# Revit family: Essentials Cupoard
name_source: partatom
category: Furniture
revit_build: Autodesk Revit 2018 (Build: 20190510_1515(x64)
units: mm (PartAtom-declared; Revit-internal decimal feet)

## family parameters
Always vertical = Yes
Cut with Voids When Loaded = No
OmniClass Number = 23.40.20.00
OmniClass Title = General Furniture and Specialties
Room Calculation Point = No
Shared = No
Work Plane-Based = No

## types (19) — shared parameters
Colour = Classic
Compliance Standards Certification = BS EN 14073-2:2004 Parts 2 and 3 and BS EN 14074:2004
Depth = 470 mm  [stored 1.54199 ft]
Expected Life = >5 years
Finish = Powder coated Steel
Manufacturer = Bisley
Range = Essentals
Revision = V1
Routine Maintenance = We recommend you clean your unit with warm water and a mild detergent solution. A damp cloth can be used to remove dust particles.
Uniclass 2015 Code = PR_40_30_78_57
Uniclass2015Title = Shelves and Storage Units
Uniclass2015Version = V1.13
Warranty = 5 Years

## per-type parameters (varying)
| type | Carcass Size | Carcass_Material | Door size | Door_Material | Height | Model | Model Reference | URL | Width |
| YECB0807 | Carcass : YECB0807 | Steel, Mild | Doors : YECB0807 | Steel, Mild | 693 mm  [stored 2.27362 ft] | YECB0907 | YECB0907 | www.bisley.com | 800 mm  [stored 2.62467 ft] |
| YECBDH0807 | Carcass : YECBDH0807 | Steel, Mild | Doors : YECBDH0807 | Steel, Mild | 718 mm  [stored 2.35564 ft] | YECB0807 | YECB0807 | www.bisley.com | 800 mm  [stored 2.62467 ft] |
| YECB0810 | Carcass : YECB0810 | Steel, Mild | Doors : YECB0810 | Steel, Mild | 1000 mm  [stored 3.28084 ft] | YECB0810 | YECB0810 | WWW.BISLEY.COM | 800 mm  [stored 2.62467 ft] |
| YECB0811 | Carcass : YECB0811 | Steel, Mild | Doors : YECB0811 | Steel, Mild | 1070 mm  [stored 3.5105 ft] | YECB0811 | YECB0811 | www.bisley.com | 800 mm  [stored 2.62467 ft] |
| YECB0812 | Carcass : YECB0812 | Steel, Mild | Doors : YECB0812 | Steel, Mild | 1270 mm | YECB0812 | YECB0812 | www.bisley.com | 800 mm  [stored 2.62467 ft] |
| YECB0815 | Carcass : YECB0815 | Steel, Mild | Doors : YECB0815 | Steel, Mild | 1570 mm | YECB0815 | YECB0815 | www.bisley.com | 800 mm  [stored 2.62467 ft] |
| YECB0819 | Carcass : YECB0819 | Steel, Mild | Doors : YECB0819 | Steel, Mild | 1970 mm  [stored 6.46325 ft] | YECB0919 | YECB0919 | www.bisley.com | 800 mm  [stored 2.62467 ft] |
| YECB0910 | Carcass : YECB0910 | <By Category> | Doors : YECB0910 | <By Category> | 1000 mm  [stored 3.28084 ft] | YECB0910 | YECB0910 | www.bisley.com | 900 mm  [stored 2.95276 ft] |
| YECB0911 | Carcass : YECB0911 | Steel, Mild | Doors : YECB0911 | Steel, Mild | 1070 mm  [stored 3.5105 ft] | YECB0911 | YECB0911 | www.bisley.com | 900 mm  [stored 2.95276 ft] |
| YECB0912 | Carcass : YECB0912 | Steel, Mild | Doors : YECB0912 | Steel, Mild | 1270 mm | YECB0912 | YECB0912 | www.bisley.com | 900 mm  [stored 2.95276 ft] |
| YECB0915 | Carcass : YECB0915 | Steel, Mild | Doors : YECB0915 | Steel, Mild | 1570 mm | YECB0915 | YECB0915 | www.bisley.com | 900 mm  [stored 2.95276 ft] |
| YECB0919 | Carcass : YECB0919 | Steel, Mild | Doors : YECB0919 | Steel, Mild | 1970 mm  [stored 6.46325 ft] | YECB0919 | YECB0919 | www.bisley.com | 900 mm  [stored 2.95276 ft] |
| YECB1007 | Carcass : YECB1007 | Steel, Mild | Doors : YECB1007 | Steel, Mild | 693 mm  [stored 2.27362 ft] | YECB1007 | YECB1007 | www.bisley.com | 1000 mm  [stored 3.28084 ft] |
| YECBDH1007 | Carcass : YECBDH1007 | Steel, Mild | Doors : YECBDH1007 | Steel, Mild | 718 mm  [stored 2.35564 ft] | YECB1007 | YECB1007 | www.bisley.com | 1000 mm  [stored 3.28084 ft] |
| YECB1010 | Carcass : YECB1010 | Steel, Mild | Doors : YECB1010 | Steel, Mild | 1000 mm  [stored 3.28084 ft] | YECB1010 | YECB1010 | www.bisley.com | 1000 mm  [stored 3.28084 ft] |
| YECB1011 | Carcass : YECB1011 | Steel, Mild | Doors : YECB1011 | Steel, Mild | 1070 mm  [stored 3.5105 ft] | YECB1011 | YECB1011 | www.bisley.com | 1000 mm  [stored 3.28084 ft] |
| YECB1012 | Carcass : YECB1012 | Steel, Mild | Doors : YECB1012 | Steel, Mild | 1270 mm | YECB1012 | YECB1012 | www.bisley.com | 1000 mm  [stored 3.28084 ft] |
| YECB1015 | Carcass : YECB1015 | Steel, Mild | Doors : YECB1015 | Steel, Mild | 1570 mm | YECB1015 | YECB1015 | www.bisley.com | 1000 mm  [stored 3.28084 ft] |
| YECB1019 | Carcass : YECB1019 | Steel, Mild | Doors : YECB1019 | Steel, Mild | 1970 mm  [stored 6.46325 ft] | YECB1019 | YECB1019 | www.bisley.com | 1000 mm  [stored 3.28084 ft] |

note: [stored X ft] marks values corroborated as IEEE doubles in the binary element streams (Revit-internal decimal feet)

## geometry (parser evidence)
native form markers: Sweep x11
no freeform markers — native parametric forms only
